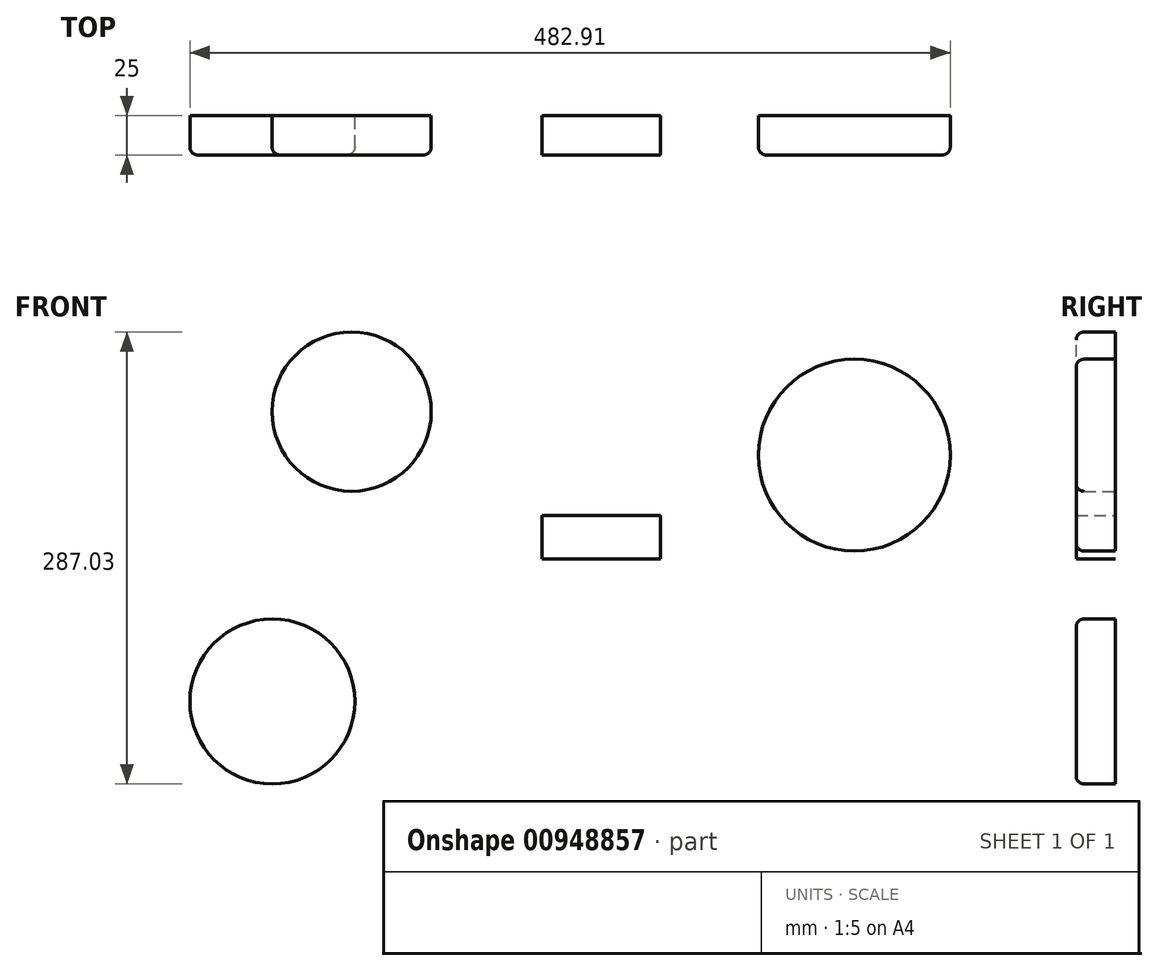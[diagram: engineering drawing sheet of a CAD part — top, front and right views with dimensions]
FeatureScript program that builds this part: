
annotation { "Feature Type Name" : "Feature", "Feature Type Description" : "" }
export const myFeature = defineFeature(function(context is Context, id is Id, definition is map)
    precondition{}
    {
        {
            var Q0;
            Q0=qCreatedBy(makeId("Front.planeOp"),FACE);
            var sketch = newSketch(context, id + "F0", { "sketchPlane" : qUnion([Q0])});
            skLineSegment(sketch, "E0.bottom", {"start": v(-45.7, 17.62) * mm, "end": v(29.28, 17.62) * mm});
            skLineSegment(sketch, "E0.top", {"start": v(-45.7, -9.96) * mm, "end": v(29.28, -9.96) * mm});
            skLineSegment(sketch, "E0.left", {"start": v(-45.7, 17.62) * mm, "end": v(-45.7, -9.96) * mm});
            skLineSegment(sketch, "E0.right", {"start": v(29.28, 17.62) * mm, "end": v(29.28, -9.96) * mm});
            skSolve(sketch);
        }
        {
            var Q0;
            Q0 = qSketchRegion(id + "F0", true);
            extrude(context, id + "F1", {"entities" : qUnion([Q0]), "depth" : 25 * mm, "offsetDistance" : 25 * mm});
        }
        {
            var Q0;
            Q0=qCreatedBy(makeId("Front.planeOp"),FACE);
            var sketch = newSketch(context, id + "F2", { "sketchPlane" : qUnion([Q0])});
            skCircle(sketch, "E1", {"center": v(152.5, 56.09) * mm, "radius": 60.92 * mm});
            skCircle(sketch, "E2", {"center": v(-166.74, 83.72) * mm, "radius": 50.56 * mm});
            skCircle(sketch, "E3", {"center": v(-217.1, -100.37) * mm, "radius": 52.38 * mm});
            skSolve(sketch);
        }
        {
            var Q0;
            Q0 = qSketchRegion(id + "F2", true);
            extrude(context, id + "F3", {"entities" : qUnion([Q0]), "depth" : 25 * mm, "offsetDistance" : 25 * mm});
        }
        {
            var Q0;
            Q0=makeQuery(id+"F3.opExtrude","CAP_FACE",FACE,{"disambiguationData":[OSD([sQuery(id+"F2.wireOp",EDGE,"E3")])],"isStart":false});
            var Q1;
            Q1=makeQuery(id+"F3.opExtrude","CAP_FACE",FACE,{"disambiguationData":[OSD([sQuery(id+"F2.wireOp",EDGE,"E2")])],"isStart":false});
            var Q2;
            Q2=makeQuery(id+"F3.opExtrude","CAP_FACE",FACE,{"disambiguationData":[OSD([sQuery(id+"F2.wireOp",EDGE,"E1")])],"isStart":false});
            fillet(context, id + "F4", {"entities" : qUnion([Q0, Q1, Q2]), "radius" : 5 * mm, "tangentPropagation" : true, "allowEdgeOverflow" : false});
        }
    });
